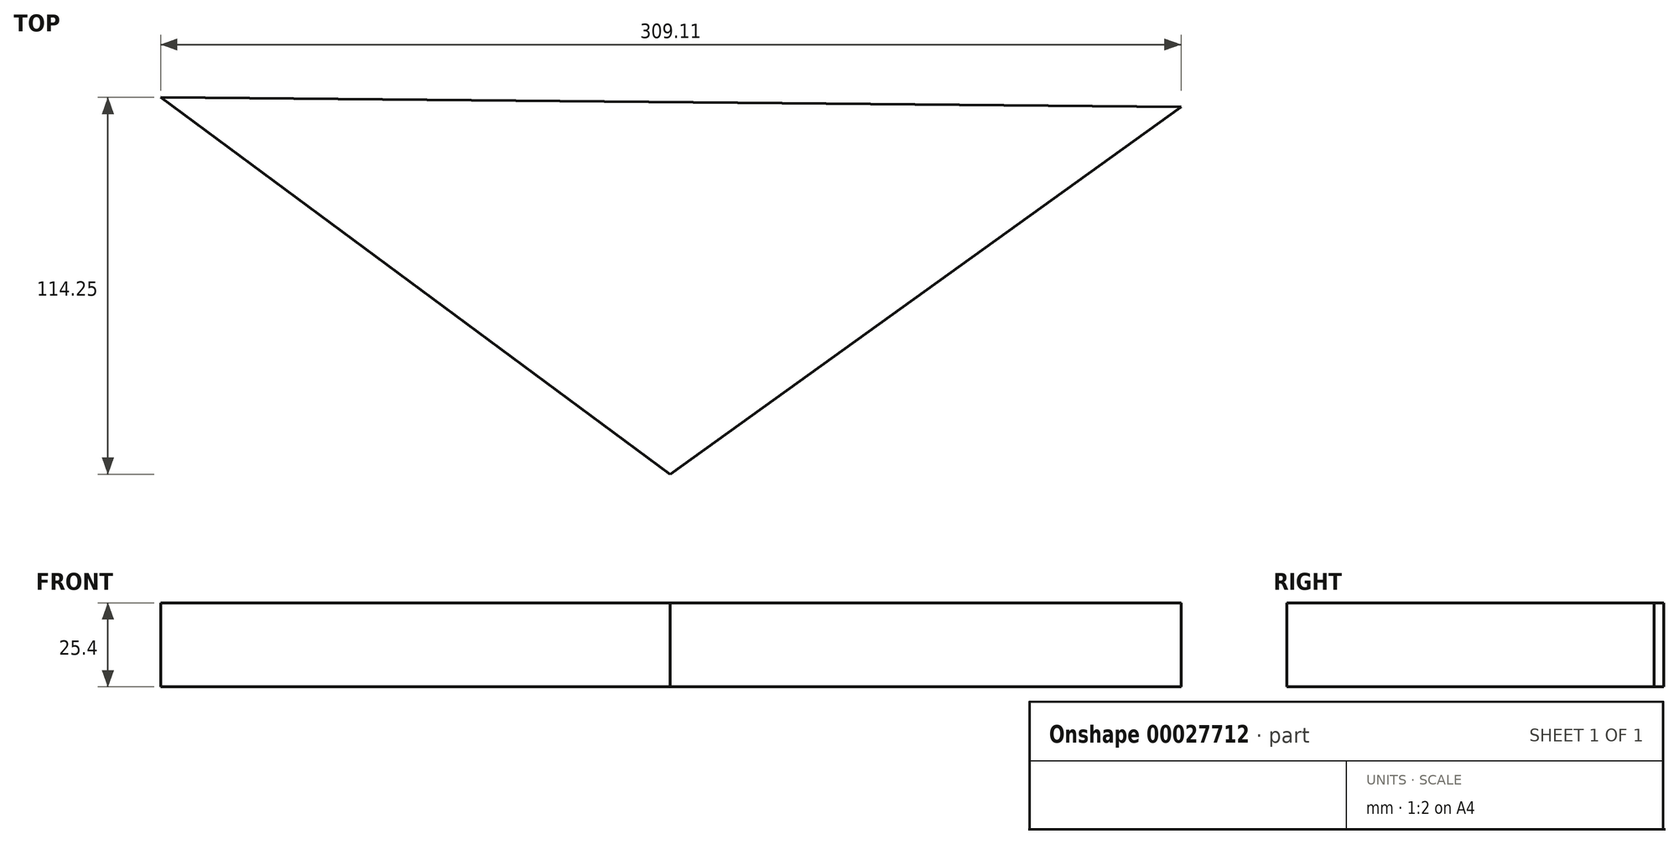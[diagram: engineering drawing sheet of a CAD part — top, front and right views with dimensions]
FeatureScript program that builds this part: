
annotation { "Feature Type Name" : "Feature", "Feature Type Description" : "" }
export const myFeature = defineFeature(function(context is Context, id is Id, definition is map)
    precondition{}
    {
        {
            var Q0;
            Q0=qCreatedBy(makeId("Top.planeOp"),FACE);
            var sketch = newSketch(context, id + "F0", { "sketchPlane" : qUnion([Q0])});
            skLineSegment(sketch, "E0", {"start": v(-154.34, -86.4) * mm, "end": v(0, -200.64) * mm});
            skLineSegment(sketch, "E1", {"start": v(0, -200.64) * mm, "end": v(154.77, -89.33) * mm});
            skLineSegment(sketch, "E2", {"start": v(154.77, -89.33) * mm, "end": v(-154.34, -86.4) * mm});
            skLineSegment(sketch, "E3", {"start": v(0, -200.64) * mm, "end": v(0, 0) * mm});
            skLineSegment(sketch, "E4", {"start": v(0, 0) * mm, "end": v(0, 83.25) * mm});
            skSolve(sketch);
        }
        {
            var Q0;
            Q0 = qSketchRegion(id + "F0IhWO2oih3wu5S_0", true);
            var Q1;
            Q1 = qSketchRegion(id + "F0", true);
            extrude(context, id + "F1", {"entities" : qUnion([Q0, Q1]), "depth" : 25.4 * mm});
        }
    });
